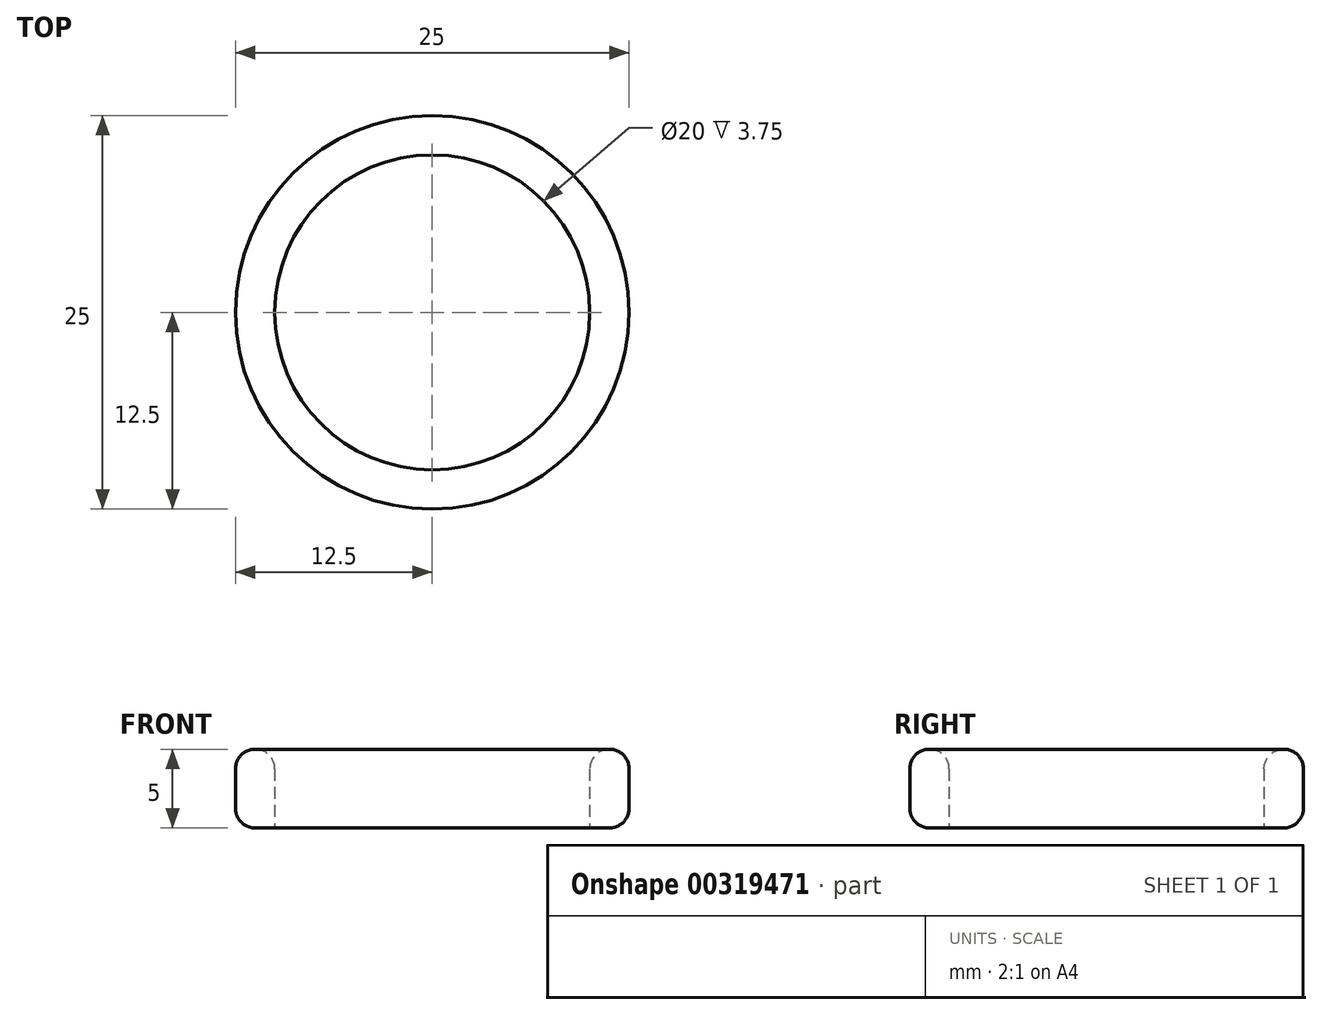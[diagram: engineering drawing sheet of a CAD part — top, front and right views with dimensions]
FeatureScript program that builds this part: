
annotation { "Feature Type Name" : "Feature", "Feature Type Description" : "" }
export const myFeature = defineFeature(function(context is Context, id is Id, definition is map)
    precondition{}
    {
        {
            var Q0;
            Q0=qCreatedBy(makeId("Top.planeOp"),FACE);
            var sketch = newSketch(context, id + "F0", { "sketchPlane" : qUnion([Q0])});
            skCircle(sketch, "E0", {"center": v(0, 0) * mm, "radius": 12.5 * mm});
            skCircle(sketch, "E1", {"center": v(0, 0) * mm, "radius": 10 * mm});
            skSolve(sketch);
        }
        {
            var Q0;
            Q0 = qSketchRegion(id + "F0", true);
            extrude(context, id + "F1", {"entities" : qUnion([Q0]), "depth" : 5 * mm});
        }
        {
            var Q0;
            Q0=makeQuery(id+"F1.opExtrude","CAP_EDGE",EDGE,{"disambiguationData":[OSD([sQuery(id+"F0.wireOp",EDGE,"E1")])],"isStart":false});
            var Q1;
            Q1=makeQuery(id+"F1.opExtrude","CAP_EDGE",EDGE,{"disambiguationData":[OSD([sQuery(id+"F0.wireOp",EDGE,"E0")])],"isStart":false});
            var Q2;
            Q2=makeQuery(id+"F1.opExtrude","CAP_EDGE",EDGE,{"disambiguationData":[OSD([sQuery(id+"F0.wireOp",EDGE,"E0")])],"isStart":true});
            var Q3;
            Q3=makeQuery(id+"F1.opExtrude","SWEPT_FACE",FACE,{"disambiguationData":[OSD([sQuery(id+"F0.wireOp",EDGE,"E0")])]});
            fillet(context, id + "F2", {"entities" : qUnion([Q0, Q1, Q2, Q3]), "radius" : 1.25 * mm, "tangentPropagation" : true, "allowEdgeOverflow" : false});
        }
    });
